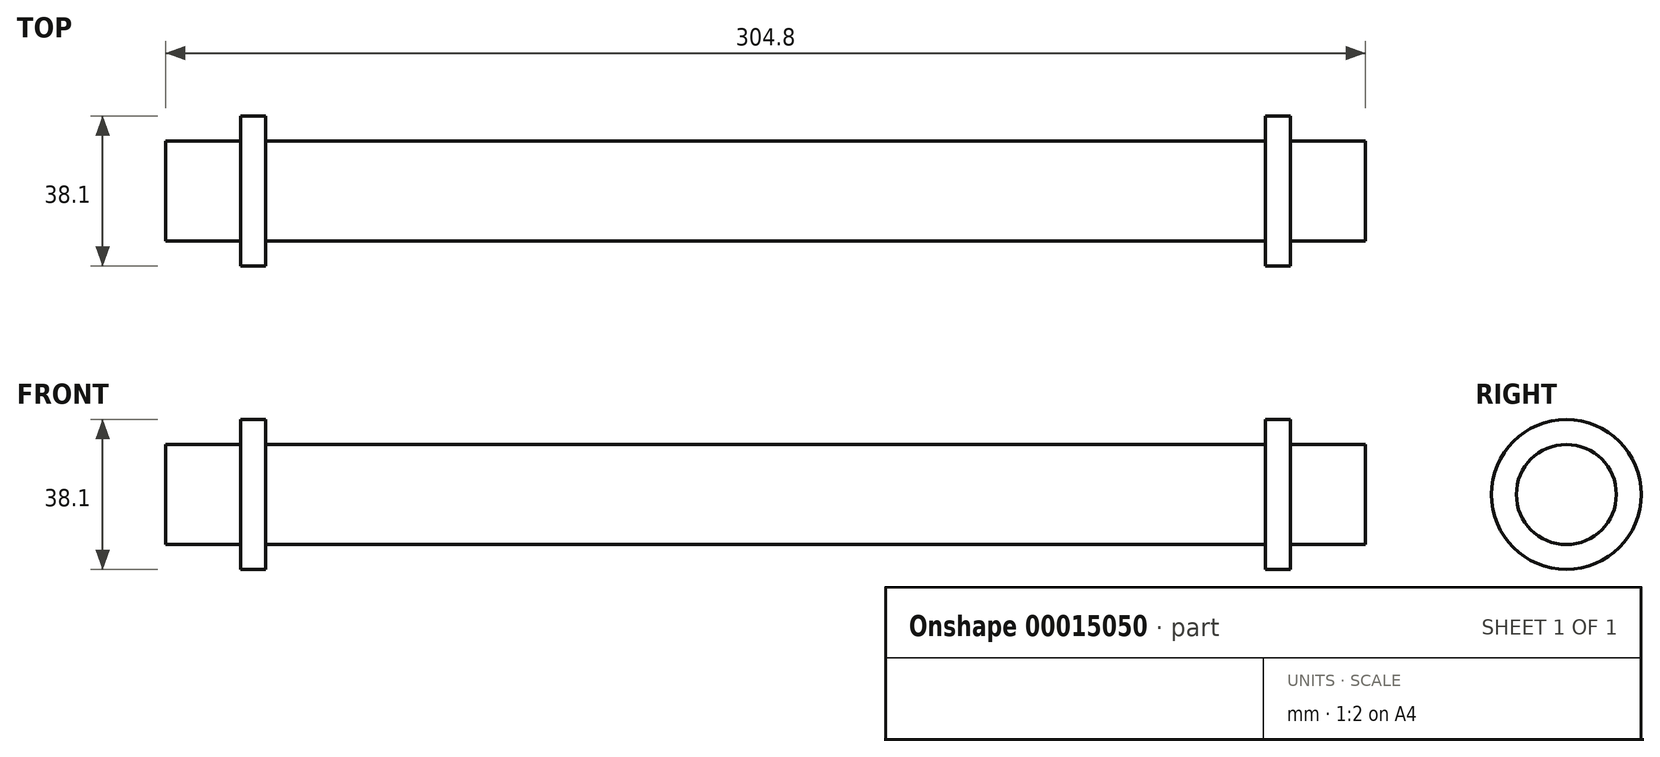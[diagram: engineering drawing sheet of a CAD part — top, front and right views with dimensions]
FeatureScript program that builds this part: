
annotation { "Feature Type Name" : "Feature", "Feature Type Description" : "" }
export const myFeature = defineFeature(function(context is Context, id is Id, definition is map)
    precondition{}
    {
        {
            var Q0;
            Q0=qCreatedBy(makeId("Right.planeOp"),FACE);
            var sketch = newSketch(context, id + "F0", { "sketchPlane" : qUnion([Q0])});
            skCircle(sketch, "E0", {"center": v(0, 0) * mm, "radius": 12.7 * mm});
            skSolve(sketch);
        }
        {
            var Q0;
            Q0 = qSketchRegion(id + "F0", true);
            extrude(context, id + "F1", {"entities" : qUnion([Q0]), "endBound" : BoundingType.SYMMETRIC, "depth" : 304.8 * mm});
        }
        {
            var Q0;
            Q0=qCreatedBy(makeId("Front.planeOp"),FACE);
            var sketch = newSketch(context, id + "F2", { "sketchPlane" : qUnion([Q0])});
            skLineSegment(sketch, "E1.bottom", {"start": v(127, 12.7) * mm, "end": v(133.35, 12.7) * mm});
            skLineSegment(sketch, "E1.top", {"start": v(127, 19.05) * mm, "end": v(133.35, 19.05) * mm});
            skLineSegment(sketch, "E1.left", {"start": v(127, 12.7) * mm, "end": v(127, 19.05) * mm});
            skLineSegment(sketch, "E1.right", {"start": v(133.35, 12.7) * mm, "end": v(133.35, 19.05) * mm});
            skLineSegment(sketch, "E2.bottom", {"start": v(-133.35, 12.7) * mm, "end": v(-127, 12.7) * mm});
            skLineSegment(sketch, "E2.top", {"start": v(-133.35, 19.05) * mm, "end": v(-127, 19.05) * mm});
            skLineSegment(sketch, "E2.left", {"start": v(-133.35, 12.7) * mm, "end": v(-133.35, 19.05) * mm});
            skLineSegment(sketch, "E2.right", {"start": v(-127, 12.7) * mm, "end": v(-127, 19.05) * mm});
            skLineSegment(sketch, "E3", {"start": v(-152.4, 12.7) * mm, "end": v(-133.35, 12.7) * mm, "construction": true});
            skLineSegment(sketch, "E4", {"start": v(133.35, 12.7) * mm, "end": v(152.4, 12.7) * mm, "construction": true});
            skLineSegment(sketch, "E5", {"start": v(0, 0) * mm, "end": v(152.4, 0) * mm, "construction": true});
            skSolve(sketch);
        }
        {
            var Q0;
            Q0=makeQuery(id+"F2.imprint","IMPRINT",FACE,{"disambiguationData":[TD([[makeQuery(id+"F2.imprint","IMPRINT",EDGE,{"derivedFrom":sQuery(id+"F2.wireOp",EDGE,"E1.bottom")}),1.0]])]});
            var Q1;
            Q1=makeQuery(id+"F2.imprint","IMPRINT",FACE,{"disambiguationData":[TD([[makeQuery(id+"F2.imprint","IMPRINT",EDGE,{"derivedFrom":sQuery(id+"F2.wireOp",EDGE,"E2.bottom")}),1.0]])]});
            var Q2;
            Q2=sQuery(id+"F2.wireOp",EDGE,"E5");
            revolve(context, id + "F3", {"operationType" : NewBodyOperationType.ADD, "entities" : qUnion([Q0, Q1]), "axis" : qUnion([Q2]), "revolveType" : RevolveType.FULL});
        }
    });
